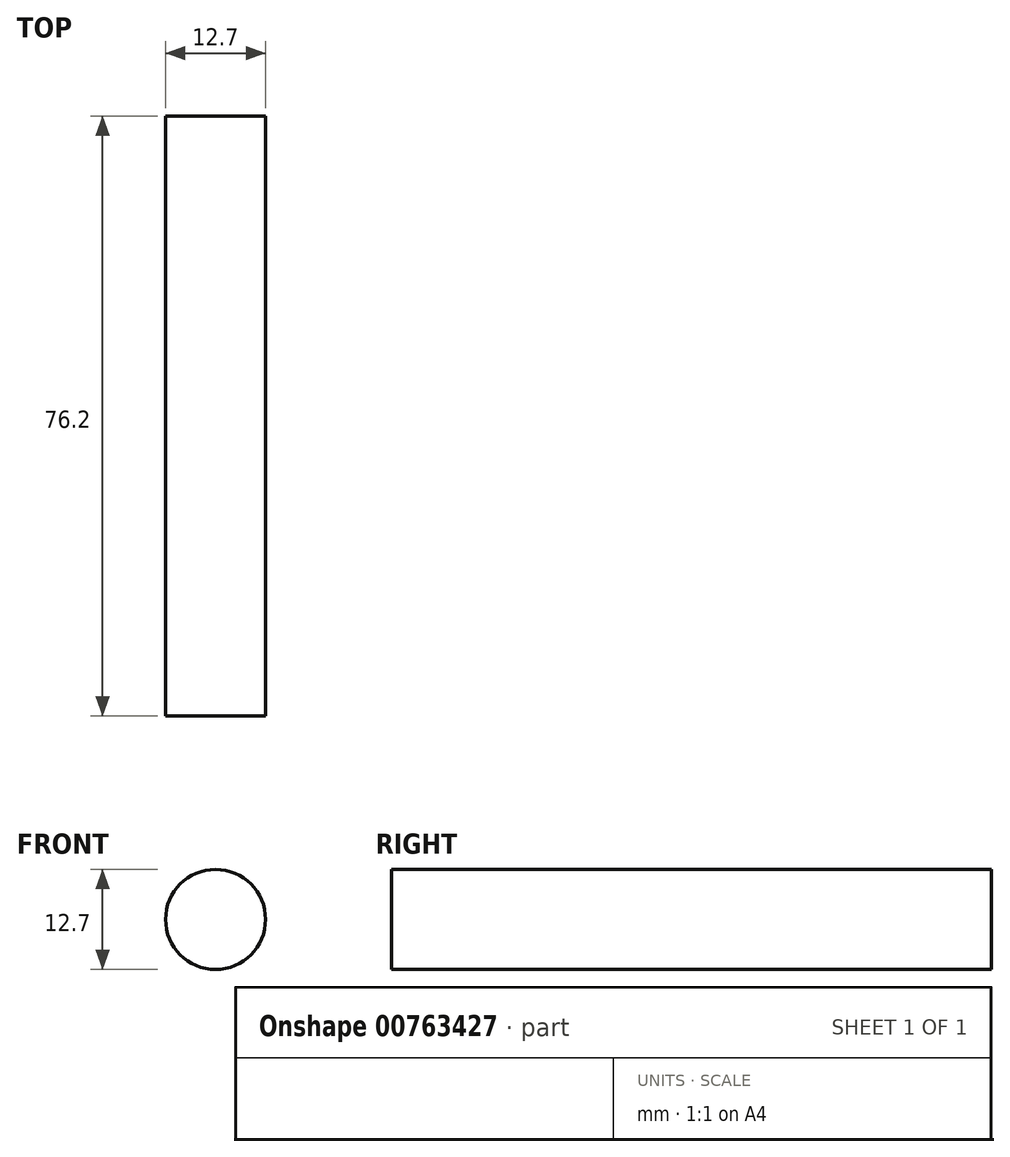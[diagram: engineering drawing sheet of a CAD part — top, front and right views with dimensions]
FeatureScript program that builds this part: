
annotation { "Feature Type Name" : "Feature", "Feature Type Description" : "" }
export const myFeature = defineFeature(function(context is Context, id is Id, definition is map)
    precondition{}
    {
        {
            var Q0;
            Q0=qCreatedBy(makeId("Front.planeOp"),FACE);
            var sketch = newSketch(context, id + "F0", { "sketchPlane" : qUnion([Q0])});
            skCircle(sketch, "E0", {"center": v(0, 0) * mm, "radius": 6.35 * mm});
            skSolve(sketch);
        }
        {
            var Q0;
            Q0 = qSketchRegion(id + "F0", true);
            extrude(context, id + "F1", {"entities" : qUnion([Q0]), "depth" : 50.8 * mm, "offsetDistance" : 25.4 * mm});
        }
        {
            var Q0;
            Q0=makeQuery(id+"F1.opExtrude","CAP_FACE",FACE,{"disambiguationData":[OSD([sQuery(id+"F0.wireOp",EDGE,"E0")])],"isStart":true});
            extrude(context, id + "F2", {"entities" : qUnion([Q0]), "operationType" : NewBodyOperationType.ADD, "depth" : 25.4 * mm, "offsetDistance" : 25.4 * mm});
        }
    });
